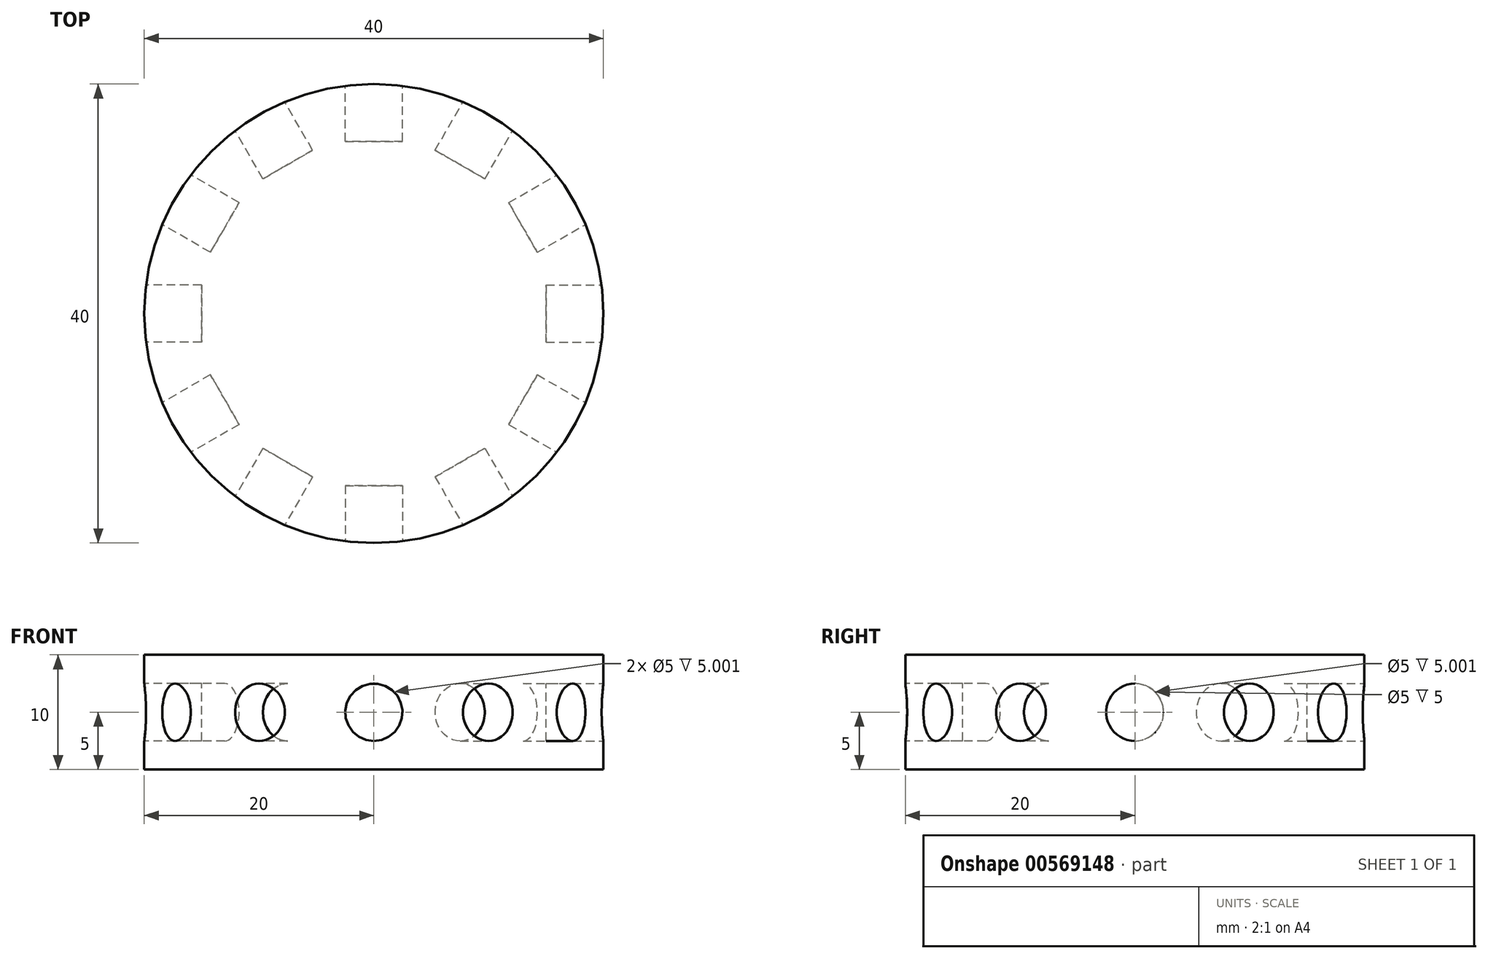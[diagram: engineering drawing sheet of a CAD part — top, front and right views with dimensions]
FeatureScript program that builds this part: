
annotation { "Feature Type Name" : "Feature", "Feature Type Description" : "" }
export const myFeature = defineFeature(function(context is Context, id is Id, definition is map)
    precondition{}
    {
        {
            var Q0;
            Q0=qCreatedBy(makeId("Top.planeOp"),FACE);
            var sketch = newSketch(context, id + "F0", { "sketchPlane" : qUnion([Q0])});
            skCircle(sketch, "E0", {"center": v(0, 0) * mm, "radius": 20 * mm});
            skSolve(sketch);
        }
        {
            var Q0;
            Q0 = qSketchRegion(id + "F0", true);
            extrude(context, id + "F1", {"entities" : qUnion([Q0]), "flatOperationType" : FlatOperationType.REMOVE, "depth" : 10 * mm, "offsetDistance" : 25 * mm, "domain" : OperationDomain.MODEL});
        }
        {
            var Q0;
            Q0=qCreatedBy(makeId("Front.planeOp"),FACE);
            cPlane(context, id + "F2", {"entities" : qUnion([Q0]), "cplaneType" : CPlaneType.OFFSET, "offset" : 20 * mm, "width" : 150 * mm, "height" : 150 * mm});
        }
        {
            var Q0;
            Q0=qCreatedBy(id+"F2.planeOp",FACE);
            var sketch = newSketch(context, id + "F3", { "sketchPlane" : qUnion([Q0])});
            skLineSegment(sketch, "E1", {"start": v(0, 0) * mm, "end": v(0, 10) * mm, "construction": true});
            skPoint(sketch, "E2", {"position": v(0, 5) * mm});
            skCircle(sketch, "E3", {"center": v(0, 5) * mm, "radius": 2.5 * mm});
            skSolve(sketch);
        }
        {
            var Q0;
            Q0=makeQuery(id+"F3.imprint","IMPRINT",FACE,{"disambiguationData":[TD([[makeQuery(id+"F3.imprint","IMPRINT",EDGE,{"derivedFrom":sQuery(id+"F3.wireOp",EDGE,"E3")}),1.0]])]});
            extrude(context, id + "F4", {"entities" : qUnion([Q0]), "oppositeDirection" : true, "depth" : 5 * mm, "offsetDistance" : 25 * mm});
        }
        {
            var Q0;
            Q0=qCreatedBy(makeId("Front.planeOp"),FACE);
            var sketch = newSketch(context, id + "F5", { "sketchPlane" : qUnion([Q0])});
            skLineSegment(sketch, "E4", {"start": v(0, 50) * mm, "end": v(0, -50) * mm, "construction": true});
            skSolve(sketch);
        }
        {
            var Q0;
            Q0=makeQuery(id+"F4.opExtrude","SWEPT_BODY",BODY,{"disambiguationData":[OSD([sQuery(id+"F3.wireOp",EDGE,"E3")])]});
            var Q1;
            Q1=sQuery(id+"F5.wireOp",EDGE,"E4");
            circularPattern(context, id + "F6", {"entities" : qUnion([Q0]), "axis" : qUnion([Q1]), "angle" : 360 * degree, "instanceCount" : 12, "equalSpace" : true, "fullFeaturePattern" : false, "computeTransformsWithoutBuiltin" : true});
        }
        {
            var Q0;
            Q0=makeQuery(id+"F6.opPattern","COPY",BODY,{"derivedFrom":makeQuery(id+"F4.opExtrude","SWEPT_BODY",BODY,{"disambiguationData":[OSD([sQuery(id+"F3.wireOp",EDGE,"E3")])]}),"instanceName":"2"});
            var Q1;
            Q1=makeQuery(id+"F6.opPattern","COPY",BODY,{"derivedFrom":makeQuery(id+"F4.opExtrude","SWEPT_BODY",BODY,{"disambiguationData":[OSD([sQuery(id+"F3.wireOp",EDGE,"E3")])]}),"instanceName":"1"});
            var Q2;
            Q2=makeQuery(id+"F4.opExtrude","SWEPT_BODY",BODY,{"disambiguationData":[OSD([sQuery(id+"F3.wireOp",EDGE,"E3")])]});
            var Q3;
            Q3=makeQuery(id+"F6.opPattern","COPY",BODY,{"derivedFrom":makeQuery(id+"F4.opExtrude","SWEPT_BODY",BODY,{"disambiguationData":[OSD([sQuery(id+"F3.wireOp",EDGE,"E3")])]}),"instanceName":"11"});
            var Q4;
            Q4=makeQuery(id+"F6.opPattern","COPY",BODY,{"derivedFrom":makeQuery(id+"F4.opExtrude","SWEPT_BODY",BODY,{"disambiguationData":[OSD([sQuery(id+"F3.wireOp",EDGE,"E3")])]}),"instanceName":"3"});
            var Q5;
            Q5=makeQuery(id+"F6.opPattern","COPY",BODY,{"derivedFrom":makeQuery(id+"F4.opExtrude","SWEPT_BODY",BODY,{"disambiguationData":[OSD([sQuery(id+"F3.wireOp",EDGE,"E3")])]}),"instanceName":"9"});
            var Q6;
            Q6=makeQuery(id+"F6.opPattern","COPY",BODY,{"derivedFrom":makeQuery(id+"F4.opExtrude","SWEPT_BODY",BODY,{"disambiguationData":[OSD([sQuery(id+"F3.wireOp",EDGE,"E3")])]}),"instanceName":"10"});
            var Q7;
            Q7=makeQuery(id+"F6.opPattern","COPY",BODY,{"derivedFrom":makeQuery(id+"F4.opExtrude","SWEPT_BODY",BODY,{"disambiguationData":[OSD([sQuery(id+"F3.wireOp",EDGE,"E3")])]}),"instanceName":"8"});
            var Q8;
            Q8=makeQuery(id+"F6.opPattern","COPY",BODY,{"derivedFrom":makeQuery(id+"F4.opExtrude","SWEPT_BODY",BODY,{"disambiguationData":[OSD([sQuery(id+"F3.wireOp",EDGE,"E3")])]}),"instanceName":"4"});
            var Q9;
            Q9=makeQuery(id+"F6.opPattern","COPY",BODY,{"derivedFrom":makeQuery(id+"F4.opExtrude","SWEPT_BODY",BODY,{"disambiguationData":[OSD([sQuery(id+"F3.wireOp",EDGE,"E3")])]}),"instanceName":"5"});
            var Q10;
            Q10=makeQuery(id+"F6.opPattern","COPY",BODY,{"derivedFrom":makeQuery(id+"F4.opExtrude","SWEPT_BODY",BODY,{"disambiguationData":[OSD([sQuery(id+"F3.wireOp",EDGE,"E3")])]}),"instanceName":"6"});
            var Q11;
            Q11=makeQuery(id+"F6.opPattern","COPY",BODY,{"derivedFrom":makeQuery(id+"F4.opExtrude","SWEPT_BODY",BODY,{"disambiguationData":[OSD([sQuery(id+"F3.wireOp",EDGE,"E3")])]}),"instanceName":"7"});
            var Q12;
            Q12=makeQuery(id+"F1.opExtrude","SWEPT_BODY",BODY,{"disambiguationData":[OSD([sQuery(id+"F0.wireOp",EDGE,"E0")])]});
            booleanBodies(context, id + "F7", {"operationType" : BooleanOperationType.SUBTRACTION, "tools" : qUnion([Q0, Q1, Q2, Q3, Q4, Q5, Q6, Q7, Q8, Q9, Q10, Q11]), "targets" : qUnion([Q12])});
        }
    });
